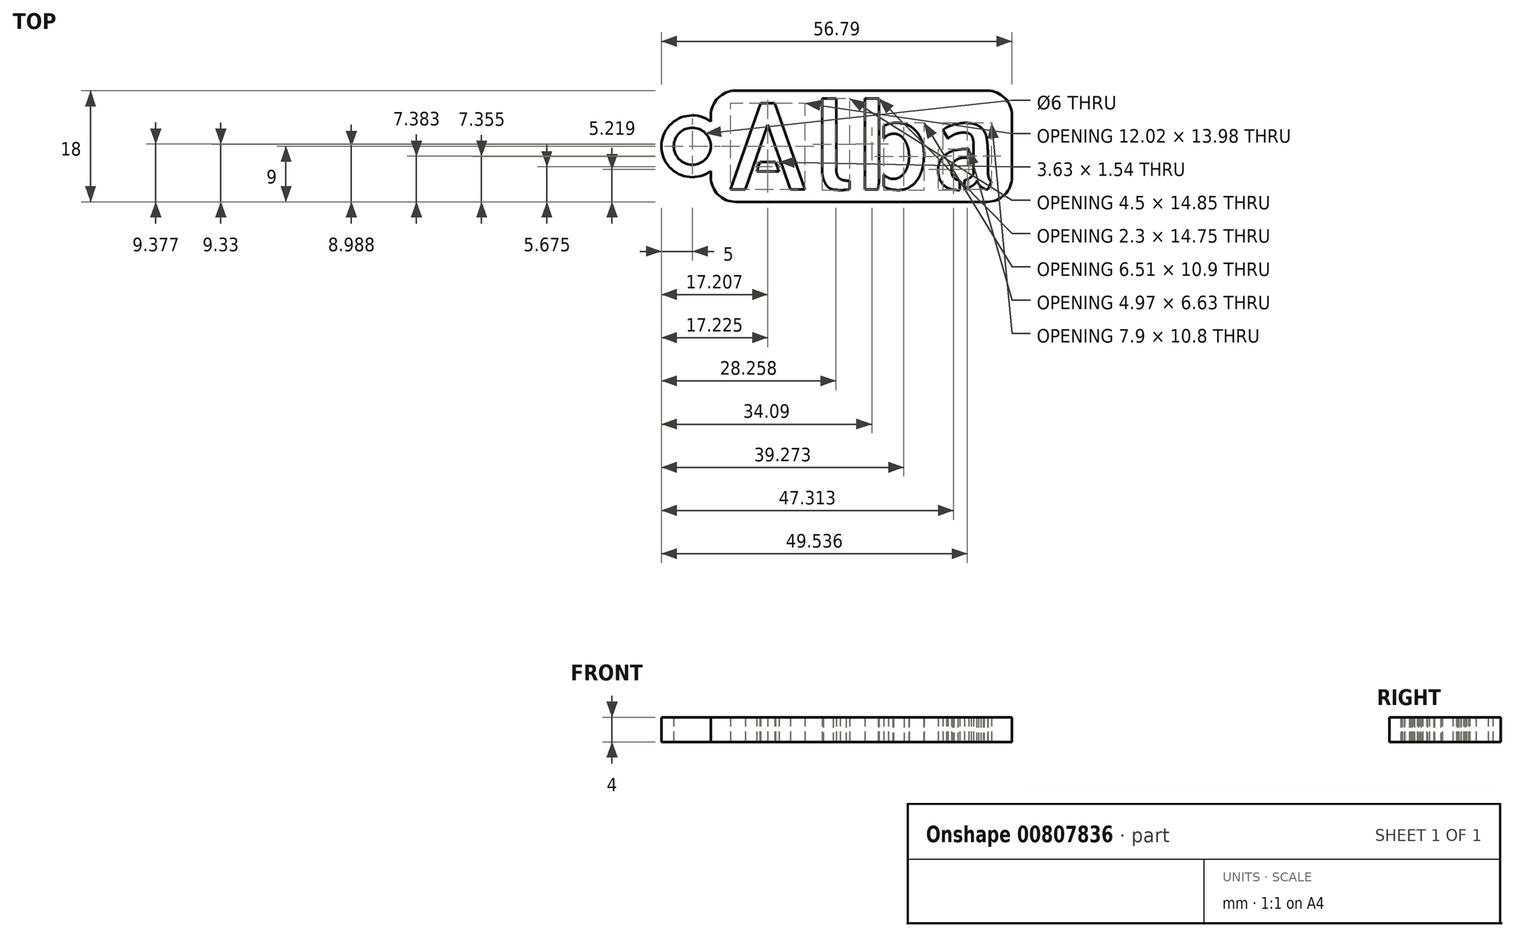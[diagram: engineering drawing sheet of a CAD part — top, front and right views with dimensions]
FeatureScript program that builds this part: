
annotation { "Feature Type Name" : "Feature", "Feature Type Description" : "" }
export const myFeature = defineFeature(function(context is Context, id is Id, definition is map)
    precondition{}
    {
        {
            var Q0;
            Q0=qCreatedBy(makeId("Top.planeOp"),FACE);
            var sketch = newSketch(context, id + "F0", { "sketchPlane" : qUnion([Q0])});
            skLineSegment(sketch, "E0.bottom", {"start": v(-2, -2) * mm, "end": v(46.79, -2) * mm});
            skLineSegment(sketch, "E0.top", {"start": v(-2, 16) * mm, "end": v(46.79, 16) * mm});
            skLineSegment(sketch, "E0.left", {"start": v(-2, -2) * mm, "end": v(-2, 3) * mm});
            skLineSegment(sketch, "E0.right", {"start": v(46.79, -2) * mm, "end": v(46.79, 16) * mm});
            skArc(sketch, "E1", {"start": v(-2, 11) * mm, "mid": v(-10, 7) * mm, "end": v(-2, 3) * mm});
            skLineSegment(sketch, "E2.trimOffspring", {"start": v(-2, 11) * mm, "end": v(-2, 16) * mm});
            skCircle(sketch, "E3", {"center": v(-5, 7) * mm, "radius": 3 * mm});
            skLineSegment(sketch, "E4", {"start": v(46.79, 7) * mm, "end": v(-10, 7) * mm, "construction": true});
            skText(sketch, "E5", { "text": "Alba", "fontName": "AllertaStencil-Regular.ttf"});
            const initialGuessF0  = {"E5": [0, 0, 1, 0, 0.014]};
            skSetInitialGuess(sketch, initialGuessF0);
            skSolve(sketch);
        }
        {
            var Q0;
            Q0=makeQuery(id+"F0.imprint","IMPRINT",FACE,{"disambiguationData":[TD([[makeQuery(id+"F0.imprint","IMPRINT",EDGE,{"derivedFrom":sQuery(id+"F0.wireOp",EDGE,"E0.bottom")}),1.0]])]});
            extrude(context, id + "F1", {"entities" : qUnion([Q0]), "depth" : 4 * mm, "offsetDistance" : 25 * mm});
        }
        {
            var Q0;
            Q0=makeQuery(id+"F1.opExtrude","SWEPT_EDGE",EDGE,{"disambiguationData":[OSD([sQuery(id+"F0.wireOp",EDGE,"E0.bottom"),sQuery(id+"F0.wireOp",EDGE,"E0.left")])]});
            var Q1;
            Q1=makeQuery(id+"F1.opExtrude","SWEPT_EDGE",EDGE,{"disambiguationData":[OSD([sQuery(id+"F0.wireOp",EDGE,"E0.bottom"),sQuery(id+"F0.wireOp",EDGE,"E0.right")])]});
            var Q2;
            Q2=makeQuery(id+"F1.opExtrude","SWEPT_EDGE",EDGE,{"disambiguationData":[OSD([sQuery(id+"F0.wireOp",EDGE,"E0.top"),sQuery(id+"F0.wireOp",EDGE,"E0.right")])]});
            var Q3;
            Q3=makeQuery(id+"F1.opExtrude","SWEPT_EDGE",EDGE,{"disambiguationData":[OSD([sQuery(id+"F0.wireOp",EDGE,"E0.top"),sQuery(id+"F0.wireOp",EDGE,"E2.trimOffspring")])]});
            fillet(context, id + "F2", {"entities" : qUnion([Q0, Q1, Q2, Q3]), "radius" : 4 * mm, "tangentPropagation" : true, "allowEdgeOverflow" : false});
        }
    });
